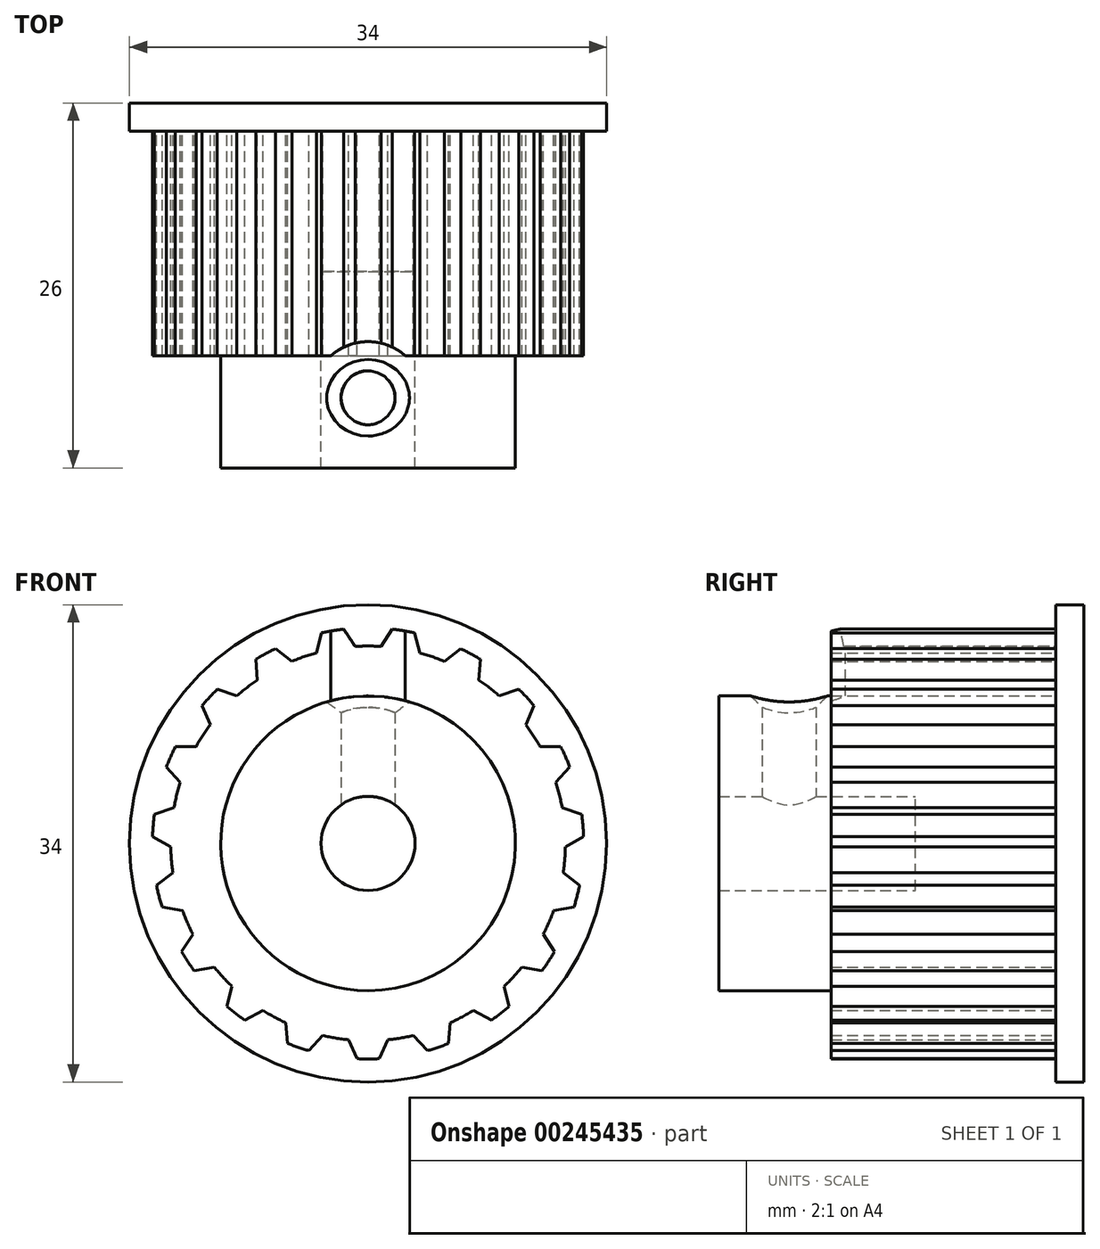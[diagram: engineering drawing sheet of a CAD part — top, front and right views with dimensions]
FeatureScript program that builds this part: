
annotation { "Feature Type Name" : "Feature", "Feature Type Description" : "" }
export const myFeature = defineFeature(function(context is Context, id is Id, definition is map)
    precondition{}
    {
        {
            var Q0;
            Q0=qCreatedBy(makeId("Front.planeOp"),FACE);
            var sketch = newSketch(context, id + "F0", { "sketchPlane" : qUnion([Q0])});
            skArc(sketch, "E0", {"start": v(1.4, -14) * mm, "mid": v(2.31, -13.87) * mm, "end": v(3.22, -13.69) * mm});
            skArc(sketch, "E1", {"start": v(-0.8, -15.34) * mm, "mid": v(0, -15.36) * mm, "end": v(0.8, -15.34) * mm});
            skLineSegment(sketch, "E2", {"start": v(0.8, -15.34) * mm, "end": v(1.4, -14) * mm});
            skLineSegment(sketch, "E3", {"start": v(-0.8, -15.34) * mm, "end": v(-1.4, -14) * mm});
            skArc(sketch, "E4.1.0", {"start": v(4.22, -14.77) * mm, "mid": v(4.99, -14.53) * mm, "end": v(5.74, -14.25) * mm});
            skLineSegment(sketch, "E4.1.1", {"start": v(5.74, -14.25) * mm, "end": v(5.87, -12.78) * mm});
            skLineSegment(sketch, "E4.1.2", {"start": v(4.22, -14.77) * mm, "end": v(3.22, -13.69) * mm});
            skArc(sketch, "E4.2.0", {"start": v(8.8, -12.6) * mm, "mid": v(9.44, -12.12) * mm, "end": v(10.05, -11.61) * mm});
            skLineSegment(sketch, "E4.2.1", {"start": v(10.05, -11.61) * mm, "end": v(9.7, -10.18) * mm});
            skLineSegment(sketch, "E4.2.2", {"start": v(8.8, -12.6) * mm, "end": v(7.5, -11.9) * mm});
            skArc(sketch, "E4.3.0", {"start": v(12.4, -9.06) * mm, "mid": v(12.86, -8.4) * mm, "end": v(13.28, -7.72) * mm});
            skLineSegment(sketch, "E4.3.1", {"start": v(13.28, -7.72) * mm, "end": v(12.48, -6.48) * mm});
            skLineSegment(sketch, "E4.3.2", {"start": v(12.4, -9.06) * mm, "end": v(10.95, -8.82) * mm});
            skArc(sketch, "E4.4.0", {"start": v(14.68, -4.54) * mm, "mid": v(14.9, -3.77) * mm, "end": v(15.07, -3) * mm});
            skLineSegment(sketch, "E4.4.1", {"start": v(15.07, -3) * mm, "end": v(13.9, -2.08) * mm});
            skLineSegment(sketch, "E4.4.2", {"start": v(14.68, -4.54) * mm, "end": v(13.22, -4.8) * mm});
            skArc(sketch, "E4.5.0", {"start": v(15.35, 0.47) * mm, "mid": v(15.3, 1.27) * mm, "end": v(15.22, 2.06) * mm});
            skLineSegment(sketch, "E4.5.1", {"start": v(15.22, 2.06) * mm, "end": v(13.83, 2.55) * mm});
            skLineSegment(sketch, "E4.5.2", {"start": v(15.35, 0.47) * mm, "end": v(14.06, -0.24) * mm});
            skArc(sketch, "E4.6.0", {"start": v(14.37, 5.43) * mm, "mid": v(14.07, 6.17) * mm, "end": v(13.73, 6.9) * mm});
            skLineSegment(sketch, "E4.6.1", {"start": v(13.73, 6.9) * mm, "end": v(12.25, 6.9) * mm});
            skLineSegment(sketch, "E4.6.2", {"start": v(14.37, 5.43) * mm, "end": v(13.38, 4.34) * mm});
            skArc(sketch, "E4.7.0", {"start": v(11.83, 9.8) * mm, "mid": v(11.3, 10.4) * mm, "end": v(10.74, 10.98) * mm});
            skLineSegment(sketch, "E4.7.1", {"start": v(10.74, 10.98) * mm, "end": v(9.35, 10.5) * mm});
            skLineSegment(sketch, "E4.7.2", {"start": v(11.83, 9.8) * mm, "end": v(11.24, 8.45) * mm});
            skArc(sketch, "E4.8.0", {"start": v(8, 13.11) * mm, "mid": v(7.31, 13.51) * mm, "end": v(6.6, 13.87) * mm});
            skLineSegment(sketch, "E4.8.1", {"start": v(6.6, 13.87) * mm, "end": v(5.43, 12.97) * mm});
            skLineSegment(sketch, "E4.8.2", {"start": v(8, 13.11) * mm, "end": v(7.89, 11.64) * mm});
            skArc(sketch, "E4.9.0", {"start": v(3.31, 15) * mm, "mid": v(2.53, 15.15) * mm, "end": v(1.74, 15.26) * mm});
            skLineSegment(sketch, "E4.9.1", {"start": v(1.74, 15.26) * mm, "end": v(0.92, 14.03) * mm});
            skLineSegment(sketch, "E4.9.2", {"start": v(3.31, 15) * mm, "end": v(3.68, 13.57) * mm});
            skArc(sketch, "E4.10.0", {"start": v(-1.74, 15.26) * mm, "mid": v(-2.53, 15.15) * mm, "end": v(-3.31, 15) * mm});
            skLineSegment(sketch, "E4.10.1", {"start": v(-3.31, 15) * mm, "end": v(-3.68, 13.57) * mm});
            skLineSegment(sketch, "E4.10.2", {"start": v(-1.74, 15.26) * mm, "end": v(-0.92, 14.03) * mm});
            skArc(sketch, "E4.11.0", {"start": v(-6.6, 13.87) * mm, "mid": v(-7.31, 13.51) * mm, "end": v(-8, 13.11) * mm});
            skLineSegment(sketch, "E4.11.1", {"start": v(-8, 13.11) * mm, "end": v(-7.89, 11.64) * mm});
            skLineSegment(sketch, "E4.11.2", {"start": v(-6.6, 13.87) * mm, "end": v(-5.43, 12.97) * mm});
            skArc(sketch, "E4.12.0", {"start": v(-10.74, 10.98) * mm, "mid": v(-11.3, 10.4) * mm, "end": v(-11.83, 9.8) * mm});
            skLineSegment(sketch, "E4.12.1", {"start": v(-11.83, 9.8) * mm, "end": v(-11.24, 8.45) * mm});
            skLineSegment(sketch, "E4.12.2", {"start": v(-10.74, 10.98) * mm, "end": v(-9.35, 10.5) * mm});
            skArc(sketch, "E4.13.0", {"start": v(-13.73, 6.9) * mm, "mid": v(-14.07, 6.17) * mm, "end": v(-14.37, 5.43) * mm});
            skLineSegment(sketch, "E4.13.1", {"start": v(-14.37, 5.43) * mm, "end": v(-13.38, 4.34) * mm});
            skLineSegment(sketch, "E4.13.2", {"start": v(-13.73, 6.9) * mm, "end": v(-12.25, 6.9) * mm});
            skArc(sketch, "E4.14.0", {"start": v(-15.22, 2.06) * mm, "mid": v(-15.3, 1.27) * mm, "end": v(-15.35, 0.47) * mm});
            skLineSegment(sketch, "E4.14.1", {"start": v(-15.35, 0.47) * mm, "end": v(-14.06, -0.24) * mm});
            skLineSegment(sketch, "E4.14.2", {"start": v(-15.22, 2.06) * mm, "end": v(-13.83, 2.55) * mm});
            skArc(sketch, "E4.15.0", {"start": v(-15.07, -3) * mm, "mid": v(-14.9, -3.77) * mm, "end": v(-14.68, -4.54) * mm});
            skLineSegment(sketch, "E4.15.1", {"start": v(-14.68, -4.54) * mm, "end": v(-13.22, -4.8) * mm});
            skLineSegment(sketch, "E4.15.2", {"start": v(-15.07, -3) * mm, "end": v(-13.9, -2.08) * mm});
            skArc(sketch, "E4.16.0", {"start": v(-13.28, -7.72) * mm, "mid": v(-12.86, -8.4) * mm, "end": v(-12.4, -9.06) * mm});
            skLineSegment(sketch, "E4.16.1", {"start": v(-12.4, -9.06) * mm, "end": v(-10.95, -8.82) * mm});
            skLineSegment(sketch, "E4.16.2", {"start": v(-13.28, -7.72) * mm, "end": v(-12.48, -6.48) * mm});
            skArc(sketch, "E4.17.0", {"start": v(-10.05, -11.61) * mm, "mid": v(-9.44, -12.12) * mm, "end": v(-8.8, -12.6) * mm});
            skLineSegment(sketch, "E4.17.1", {"start": v(-8.8, -12.6) * mm, "end": v(-7.5, -11.9) * mm});
            skLineSegment(sketch, "E4.17.2", {"start": v(-10.05, -11.61) * mm, "end": v(-9.7, -10.18) * mm});
            skArc(sketch, "E4.18.0", {"start": v(-5.74, -14.25) * mm, "mid": v(-4.99, -14.53) * mm, "end": v(-4.22, -14.77) * mm});
            skLineSegment(sketch, "E4.18.1", {"start": v(-4.22, -14.77) * mm, "end": v(-3.22, -13.69) * mm});
            skLineSegment(sketch, "E4.18.2", {"start": v(-5.74, -14.25) * mm, "end": v(-5.87, -12.78) * mm});
            skArc(sketch, "E5.trimOffspring", {"start": v(5.87, -12.78) * mm, "mid": v(6.7, -12.37) * mm, "end": v(7.5, -11.9) * mm});
            skArc(sketch, "E6.trimOffspring", {"start": v(9.7, -10.18) * mm, "mid": v(10.35, -9.52) * mm, "end": v(10.95, -8.82) * mm});
            skArc(sketch, "E7.trimOffspring", {"start": v(12.48, -6.48) * mm, "mid": v(12.88, -5.65) * mm, "end": v(13.22, -4.8) * mm});
            skArc(sketch, "E8.trimOffspring", {"start": v(-3.22, -13.69) * mm, "mid": v(-2.31, -13.87) * mm, "end": v(-1.4, -14) * mm});
            skArc(sketch, "E9.trimOffspring", {"start": v(-7.5, -11.9) * mm, "mid": v(-6.7, -12.37) * mm, "end": v(-5.87, -12.78) * mm});
            skArc(sketch, "E10.trimOffspring", {"start": v(-10.95, -8.82) * mm, "mid": v(-10.35, -9.52) * mm, "end": v(-9.7, -10.18) * mm});
            skArc(sketch, "E11.trimOffspring", {"start": v(-13.22, -4.8) * mm, "mid": v(-12.88, -5.65) * mm, "end": v(-12.48, -6.48) * mm});
            skArc(sketch, "E12.trimOffspring", {"start": v(-14.06, -0.24) * mm, "mid": v(-14.01, -1.16) * mm, "end": v(-13.9, -2.08) * mm});
            skArc(sketch, "E13.trimOffspring", {"start": v(-13.38, 4.34) * mm, "mid": v(-13.63, 3.45) * mm, "end": v(-13.83, 2.55) * mm});
            skArc(sketch, "E14.trimOffspring", {"start": v(-11.24, 8.45) * mm, "mid": v(-11.77, 7.7) * mm, "end": v(-12.25, 6.9) * mm});
            skArc(sketch, "E15.trimOffspring", {"start": v(-7.89, 11.64) * mm, "mid": v(-8.64, 11.1) * mm, "end": v(-9.35, 10.5) * mm});
            skArc(sketch, "E16.trimOffspring", {"start": v(-3.68, 13.57) * mm, "mid": v(-4.57, 13.3) * mm, "end": v(-5.43, 12.97) * mm});
            skArc(sketch, "E17.trimOffspring", {"start": v(0.92, 14.03) * mm, "mid": v(0, 14.06) * mm, "end": v(-0.92, 14.03) * mm});
            skArc(sketch, "E18.trimOffspring", {"start": v(5.43, 12.97) * mm, "mid": v(4.57, 13.3) * mm, "end": v(3.68, 13.57) * mm});
            skArc(sketch, "E19.trimOffspring", {"start": v(9.35, 10.5) * mm, "mid": v(8.64, 11.1) * mm, "end": v(7.89, 11.64) * mm});
            skArc(sketch, "E20.trimOffspring", {"start": v(12.25, 6.9) * mm, "mid": v(11.77, 7.7) * mm, "end": v(11.24, 8.45) * mm});
            skArc(sketch, "E21.trimOffspring", {"start": v(13.9, -2.08) * mm, "mid": v(14.01, -1.16) * mm, "end": v(14.06, -0.24) * mm});
            skArc(sketch, "E22.trimOffspring", {"start": v(13.83, 2.55) * mm, "mid": v(13.63, 3.45) * mm, "end": v(13.38, 4.34) * mm});
            skSolve(sketch);
        }
        {
            var Q0;
            Q0=qSketchRegion(id+"F0",true);
            extrude(context, id + "F1", {"entities" : qUnion([Q0]), "depth" : 16 * mm});
        }
        {
            var Q0;
            Q0=makeQuery(id+"F1.opExtrude","CAP_FACE",FACE,{"disambiguationData":[OSD([sQuery(id+"F0.wireOp",EDGE,"E0"),sQuery(id+"F0.wireOp",EDGE,"E1"),sQuery(id+"F0.wireOp",EDGE,"E2"),sQuery(id+"F0.wireOp",EDGE,"E3"),sQuery(id+"F0.wireOp",EDGE,"E4.1.0"),sQuery(id+"F0.wireOp",EDGE,"E4.1.1"),sQuery(id+"F0.wireOp",EDGE,"E4.1.2"),sQuery(id+"F0.wireOp",EDGE,"E4.2.0"),sQuery(id+"F0.wireOp",EDGE,"E4.2.1"),sQuery(id+"F0.wireOp",EDGE,"E4.2.2"),sQuery(id+"F0.wireOp",EDGE,"E4.3.0"),sQuery(id+"F0.wireOp",EDGE,"E4.3.1"),sQuery(id+"F0.wireOp",EDGE,"E4.3.2"),sQuery(id+"F0.wireOp",EDGE,"E4.4.0"),sQuery(id+"F0.wireOp",EDGE,"E4.4.1"),sQuery(id+"F0.wireOp",EDGE,"E4.4.2"),sQuery(id+"F0.wireOp",EDGE,"E4.5.0"),sQuery(id+"F0.wireOp",EDGE,"E4.5.1"),sQuery(id+"F0.wireOp",EDGE,"E4.5.2"),sQuery(id+"F0.wireOp",EDGE,"E4.6.0"),sQuery(id+"F0.wireOp",EDGE,"E4.6.1"),sQuery(id+"F0.wireOp",EDGE,"E4.6.2"),sQuery(id+"F0.wireOp",EDGE,"E4.7.0"),sQuery(id+"F0.wireOp",EDGE,"E4.7.1"),sQuery(id+"F0.wireOp",EDGE,"E4.7.2"),sQuery(id+"F0.wireOp",EDGE,"E4.8.0"),sQuery(id+"F0.wireOp",EDGE,"E4.8.1"),sQuery(id+"F0.wireOp",EDGE,"E4.8.2"),sQuery(id+"F0.wireOp",EDGE,"E4.9.0"),sQuery(id+"F0.wireOp",EDGE,"E4.9.1"),sQuery(id+"F0.wireOp",EDGE,"E4.9.2"),sQuery(id+"F0.wireOp",EDGE,"E4.10.0"),sQuery(id+"F0.wireOp",EDGE,"E4.10.1"),sQuery(id+"F0.wireOp",EDGE,"E4.10.2"),sQuery(id+"F0.wireOp",EDGE,"E4.11.0"),sQuery(id+"F0.wireOp",EDGE,"E4.11.1"),sQuery(id+"F0.wireOp",EDGE,"E4.11.2"),sQuery(id+"F0.wireOp",EDGE,"E4.12.0"),sQuery(id+"F0.wireOp",EDGE,"E4.12.1"),sQuery(id+"F0.wireOp",EDGE,"E4.12.2"),sQuery(id+"F0.wireOp",EDGE,"E4.13.0"),sQuery(id+"F0.wireOp",EDGE,"E4.13.1"),sQuery(id+"F0.wireOp",EDGE,"E4.13.2"),sQuery(id+"F0.wireOp",EDGE,"E4.14.0"),sQuery(id+"F0.wireOp",EDGE,"E4.14.1"),sQuery(id+"F0.wireOp",EDGE,"E4.14.2"),sQuery(id+"F0.wireOp",EDGE,"E4.15.0"),sQuery(id+"F0.wireOp",EDGE,"E4.15.1"),sQuery(id+"F0.wireOp",EDGE,"E4.15.2"),sQuery(id+"F0.wireOp",EDGE,"E4.16.0"),sQuery(id+"F0.wireOp",EDGE,"E4.16.1"),sQuery(id+"F0.wireOp",EDGE,"E4.16.2"),sQuery(id+"F0.wireOp",EDGE,"E4.17.0"),sQuery(id+"F0.wireOp",EDGE,"E4.17.1"),sQuery(id+"F0.wireOp",EDGE,"E4.17.2"),sQuery(id+"F0.wireOp",EDGE,"E4.18.0"),sQuery(id+"F0.wireOp",EDGE,"E4.18.1"),sQuery(id+"F0.wireOp",EDGE,"E4.18.2"),sQuery(id+"F0.wireOp",EDGE,"E5.trimOffspring"),sQuery(id+"F0.wireOp",EDGE,"E6.trimOffspring"),sQuery(id+"F0.wireOp",EDGE,"E7.trimOffspring"),sQuery(id+"F0.wireOp",EDGE,"E8.trimOffspring"),sQuery(id+"F0.wireOp",EDGE,"E9.trimOffspring"),sQuery(id+"F0.wireOp",EDGE,"E10.trimOffspring"),sQuery(id+"F0.wireOp",EDGE,"E11.trimOffspring"),sQuery(id+"F0.wireOp",EDGE,"E12.trimOffspring"),sQuery(id+"F0.wireOp",EDGE,"E13.trimOffspring"),sQuery(id+"F0.wireOp",EDGE,"E14.trimOffspring"),sQuery(id+"F0.wireOp",EDGE,"E15.trimOffspring"),sQuery(id+"F0.wireOp",EDGE,"E16.trimOffspring"),sQuery(id+"F0.wireOp",EDGE,"E17.trimOffspring"),sQuery(id+"F0.wireOp",EDGE,"E18.trimOffspring"),sQuery(id+"F0.wireOp",EDGE,"E19.trimOffspring"),sQuery(id+"F0.wireOp",EDGE,"E20.trimOffspring"),sQuery(id+"F0.wireOp",EDGE,"E21.trimOffspring"),sQuery(id+"F0.wireOp",EDGE,"E22.trimOffspring")])],"isStart":true});
            var sketch = newSketch(context, id + "F2", { "sketchPlane" : qUnion([Q0])});
            skCircle(sketch, "E23", {"center": v(0, 0) * mm, "radius": 17 * mm});
            skSolve(sketch);
        }
        {
            var Q0;
            Q0=qSketchRegion(id+"F2",true);
            extrude(context, id + "F3", {"entities" : qUnion([Q0]), "operationType" : NewBodyOperationType.ADD, "depth" : 2 * mm});
        }
        {
            var Q0;
            Q0=makeQuery(id+"F1.opExtrude","CAP_FACE",FACE,{"disambiguationData":[OSD([sQuery(id+"F0.wireOp",EDGE,"E0"),sQuery(id+"F0.wireOp",EDGE,"E1"),sQuery(id+"F0.wireOp",EDGE,"E2"),sQuery(id+"F0.wireOp",EDGE,"E3"),sQuery(id+"F0.wireOp",EDGE,"E4.1.0"),sQuery(id+"F0.wireOp",EDGE,"E4.1.1"),sQuery(id+"F0.wireOp",EDGE,"E4.1.2"),sQuery(id+"F0.wireOp",EDGE,"E4.2.0"),sQuery(id+"F0.wireOp",EDGE,"E4.2.1"),sQuery(id+"F0.wireOp",EDGE,"E4.2.2"),sQuery(id+"F0.wireOp",EDGE,"E4.3.0"),sQuery(id+"F0.wireOp",EDGE,"E4.3.1"),sQuery(id+"F0.wireOp",EDGE,"E4.3.2"),sQuery(id+"F0.wireOp",EDGE,"E4.4.0"),sQuery(id+"F0.wireOp",EDGE,"E4.4.1"),sQuery(id+"F0.wireOp",EDGE,"E4.4.2"),sQuery(id+"F0.wireOp",EDGE,"E4.5.0"),sQuery(id+"F0.wireOp",EDGE,"E4.5.1"),sQuery(id+"F0.wireOp",EDGE,"E4.5.2"),sQuery(id+"F0.wireOp",EDGE,"E4.6.0"),sQuery(id+"F0.wireOp",EDGE,"E4.6.1"),sQuery(id+"F0.wireOp",EDGE,"E4.6.2"),sQuery(id+"F0.wireOp",EDGE,"E4.7.0"),sQuery(id+"F0.wireOp",EDGE,"E4.7.1"),sQuery(id+"F0.wireOp",EDGE,"E4.7.2"),sQuery(id+"F0.wireOp",EDGE,"E4.8.0"),sQuery(id+"F0.wireOp",EDGE,"E4.8.1"),sQuery(id+"F0.wireOp",EDGE,"E4.8.2"),sQuery(id+"F0.wireOp",EDGE,"E4.9.0"),sQuery(id+"F0.wireOp",EDGE,"E4.9.1"),sQuery(id+"F0.wireOp",EDGE,"E4.9.2"),sQuery(id+"F0.wireOp",EDGE,"E4.10.0"),sQuery(id+"F0.wireOp",EDGE,"E4.10.1"),sQuery(id+"F0.wireOp",EDGE,"E4.10.2"),sQuery(id+"F0.wireOp",EDGE,"E4.11.0"),sQuery(id+"F0.wireOp",EDGE,"E4.11.1"),sQuery(id+"F0.wireOp",EDGE,"E4.11.2"),sQuery(id+"F0.wireOp",EDGE,"E4.12.0"),sQuery(id+"F0.wireOp",EDGE,"E4.12.1"),sQuery(id+"F0.wireOp",EDGE,"E4.12.2"),sQuery(id+"F0.wireOp",EDGE,"E4.13.0"),sQuery(id+"F0.wireOp",EDGE,"E4.13.1"),sQuery(id+"F0.wireOp",EDGE,"E4.13.2"),sQuery(id+"F0.wireOp",EDGE,"E4.14.0"),sQuery(id+"F0.wireOp",EDGE,"E4.14.1"),sQuery(id+"F0.wireOp",EDGE,"E4.14.2"),sQuery(id+"F0.wireOp",EDGE,"E4.15.0"),sQuery(id+"F0.wireOp",EDGE,"E4.15.1"),sQuery(id+"F0.wireOp",EDGE,"E4.15.2"),sQuery(id+"F0.wireOp",EDGE,"E4.16.0"),sQuery(id+"F0.wireOp",EDGE,"E4.16.1"),sQuery(id+"F0.wireOp",EDGE,"E4.16.2"),sQuery(id+"F0.wireOp",EDGE,"E4.17.0"),sQuery(id+"F0.wireOp",EDGE,"E4.17.1"),sQuery(id+"F0.wireOp",EDGE,"E4.17.2"),sQuery(id+"F0.wireOp",EDGE,"E4.18.0"),sQuery(id+"F0.wireOp",EDGE,"E4.18.1"),sQuery(id+"F0.wireOp",EDGE,"E4.18.2"),sQuery(id+"F0.wireOp",EDGE,"E5.trimOffspring"),sQuery(id+"F0.wireOp",EDGE,"E6.trimOffspring"),sQuery(id+"F0.wireOp",EDGE,"E7.trimOffspring"),sQuery(id+"F0.wireOp",EDGE,"E8.trimOffspring"),sQuery(id+"F0.wireOp",EDGE,"E9.trimOffspring"),sQuery(id+"F0.wireOp",EDGE,"E10.trimOffspring"),sQuery(id+"F0.wireOp",EDGE,"E11.trimOffspring"),sQuery(id+"F0.wireOp",EDGE,"E12.trimOffspring"),sQuery(id+"F0.wireOp",EDGE,"E13.trimOffspring"),sQuery(id+"F0.wireOp",EDGE,"E14.trimOffspring"),sQuery(id+"F0.wireOp",EDGE,"E15.trimOffspring"),sQuery(id+"F0.wireOp",EDGE,"E16.trimOffspring"),sQuery(id+"F0.wireOp",EDGE,"E17.trimOffspring"),sQuery(id+"F0.wireOp",EDGE,"E18.trimOffspring"),sQuery(id+"F0.wireOp",EDGE,"E19.trimOffspring"),sQuery(id+"F0.wireOp",EDGE,"E20.trimOffspring"),sQuery(id+"F0.wireOp",EDGE,"E21.trimOffspring"),sQuery(id+"F0.wireOp",EDGE,"E22.trimOffspring")])],"isStart":false});
            var sketch = newSketch(context, id + "F4", { "sketchPlane" : qUnion([Q0])});
            skCircle(sketch, "E24", {"center": v(0, 0) * mm, "radius": 3.35 * mm});
            skCircle(sketch, "E25", {"center": v(0, 0) * mm, "radius": 10.5 * mm});
            skSolve(sketch);
        }
        {
            var Q0;
            Q0=qSketchRegion(id+"F4",true);
            extrude(context, id + "F5", {"entities" : qUnion([Q0]), "operationType" : NewBodyOperationType.ADD, "depth" : 8 * mm});
        }
        {
            var Q0;
            Q0=makeQuery(id+"F5.boolean.opBoolean","SPLIT",FACE,{"disambiguationData":[TD([makeQuery(id+"F5.opExtrude","SWEPT_FACE",FACE,{"disambiguationData":[OSD([sQuery(id+"F4.wireOp",EDGE,"E24")])]})])],"derivedFrom":makeQuery(id+"F1.opExtrude","CAP_FACE",FACE,{"disambiguationData":[OSD([sQuery(id+"F0.wireOp",EDGE,"E0"),sQuery(id+"F0.wireOp",EDGE,"E1"),sQuery(id+"F0.wireOp",EDGE,"E2"),sQuery(id+"F0.wireOp",EDGE,"E3"),sQuery(id+"F0.wireOp",EDGE,"E4.1.0"),sQuery(id+"F0.wireOp",EDGE,"E4.1.1"),sQuery(id+"F0.wireOp",EDGE,"E4.1.2"),sQuery(id+"F0.wireOp",EDGE,"E4.2.0"),sQuery(id+"F0.wireOp",EDGE,"E4.2.1"),sQuery(id+"F0.wireOp",EDGE,"E4.2.2"),sQuery(id+"F0.wireOp",EDGE,"E4.3.0"),sQuery(id+"F0.wireOp",EDGE,"E4.3.1"),sQuery(id+"F0.wireOp",EDGE,"E4.3.2"),sQuery(id+"F0.wireOp",EDGE,"E4.4.0"),sQuery(id+"F0.wireOp",EDGE,"E4.4.1"),sQuery(id+"F0.wireOp",EDGE,"E4.4.2"),sQuery(id+"F0.wireOp",EDGE,"E4.5.0"),sQuery(id+"F0.wireOp",EDGE,"E4.5.1"),sQuery(id+"F0.wireOp",EDGE,"E4.5.2"),sQuery(id+"F0.wireOp",EDGE,"E4.6.0"),sQuery(id+"F0.wireOp",EDGE,"E4.6.1"),sQuery(id+"F0.wireOp",EDGE,"E4.6.2"),sQuery(id+"F0.wireOp",EDGE,"E4.7.0"),sQuery(id+"F0.wireOp",EDGE,"E4.7.1"),sQuery(id+"F0.wireOp",EDGE,"E4.7.2"),sQuery(id+"F0.wireOp",EDGE,"E4.8.0"),sQuery(id+"F0.wireOp",EDGE,"E4.8.1"),sQuery(id+"F0.wireOp",EDGE,"E4.8.2"),sQuery(id+"F0.wireOp",EDGE,"E4.9.0"),sQuery(id+"F0.wireOp",EDGE,"E4.9.1"),sQuery(id+"F0.wireOp",EDGE,"E4.9.2"),sQuery(id+"F0.wireOp",EDGE,"E4.10.0"),sQuery(id+"F0.wireOp",EDGE,"E4.10.1"),sQuery(id+"F0.wireOp",EDGE,"E4.10.2"),sQuery(id+"F0.wireOp",EDGE,"E4.11.0"),sQuery(id+"F0.wireOp",EDGE,"E4.11.1"),sQuery(id+"F0.wireOp",EDGE,"E4.11.2"),sQuery(id+"F0.wireOp",EDGE,"E4.12.0"),sQuery(id+"F0.wireOp",EDGE,"E4.12.1"),sQuery(id+"F0.wireOp",EDGE,"E4.12.2"),sQuery(id+"F0.wireOp",EDGE,"E4.13.0"),sQuery(id+"F0.wireOp",EDGE,"E4.13.1"),sQuery(id+"F0.wireOp",EDGE,"E4.13.2"),sQuery(id+"F0.wireOp",EDGE,"E4.14.0"),sQuery(id+"F0.wireOp",EDGE,"E4.14.1"),sQuery(id+"F0.wireOp",EDGE,"E4.14.2"),sQuery(id+"F0.wireOp",EDGE,"E4.15.0"),sQuery(id+"F0.wireOp",EDGE,"E4.15.1"),sQuery(id+"F0.wireOp",EDGE,"E4.15.2"),sQuery(id+"F0.wireOp",EDGE,"E4.16.0"),sQuery(id+"F0.wireOp",EDGE,"E4.16.1"),sQuery(id+"F0.wireOp",EDGE,"E4.16.2"),sQuery(id+"F0.wireOp",EDGE,"E4.17.0"),sQuery(id+"F0.wireOp",EDGE,"E4.17.1"),sQuery(id+"F0.wireOp",EDGE,"E4.17.2"),sQuery(id+"F0.wireOp",EDGE,"E4.18.0"),sQuery(id+"F0.wireOp",EDGE,"E4.18.1"),sQuery(id+"F0.wireOp",EDGE,"E4.18.2"),sQuery(id+"F0.wireOp",EDGE,"E5.trimOffspring"),sQuery(id+"F0.wireOp",EDGE,"E6.trimOffspring"),sQuery(id+"F0.wireOp",EDGE,"E7.trimOffspring"),sQuery(id+"F0.wireOp",EDGE,"E8.trimOffspring"),sQuery(id+"F0.wireOp",EDGE,"E9.trimOffspring"),sQuery(id+"F0.wireOp",EDGE,"E10.trimOffspring"),sQuery(id+"F0.wireOp",EDGE,"E11.trimOffspring"),sQuery(id+"F0.wireOp",EDGE,"E12.trimOffspring"),sQuery(id+"F0.wireOp",EDGE,"E13.trimOffspring"),sQuery(id+"F0.wireOp",EDGE,"E14.trimOffspring"),sQuery(id+"F0.wireOp",EDGE,"E15.trimOffspring"),sQuery(id+"F0.wireOp",EDGE,"E16.trimOffspring"),sQuery(id+"F0.wireOp",EDGE,"E17.trimOffspring"),sQuery(id+"F0.wireOp",EDGE,"E18.trimOffspring"),sQuery(id+"F0.wireOp",EDGE,"E19.trimOffspring"),sQuery(id+"F0.wireOp",EDGE,"E20.trimOffspring"),sQuery(id+"F0.wireOp",EDGE,"E21.trimOffspring"),sQuery(id+"F0.wireOp",EDGE,"E22.trimOffspring")])],"isStart":false})});
            extrude(context, id + "F6", {"entities" : qUnion([Q0]), "operationType" : NewBodyOperationType.REMOVE, "oppositeDirection" : true, "depth" : 6 * mm});
        }
        {
            var Q0;
            Q0=qCreatedBy(makeId("Top.planeOp"),FACE);
            var sketch = newSketch(context, id + "F7", { "sketchPlane" : qUnion([Q0])});
            skLineSegment(sketch, "E26", {"start": v(0, 0) * mm, "end": v(0, -15) * mm});
            skLineSegment(sketch, "E27", {"start": v(0, -15) * mm, "end": v(0, -19) * mm});
            skCircle(sketch, "E28", {"center": v(0, -19) * mm, "radius": 1.93 * mm});
            skSolve(sketch);
        }
        {
            var Q0;
            Q0=qSketchRegion(id+"F7",true);
            extrude(context, id + "F8", {"entities" : qUnion([Q0]), "operationType" : NewBodyOperationType.REMOVE, "depth" : 25 * mm});
        }
        {
            var Q0;
            Q0=makeQuery(id+"F8.boolean.opBoolean","INTERSECT",EDGE,{"derivedFrom":[makeQuery(id+"F5.opExtrude","SWEPT_FACE",FACE,{"disambiguationData":[OSD([sQuery(id+"F4.wireOp",EDGE,"E25")])]}),makeQuery(id+"F8.opExtrude","SWEPT_FACE",FACE,{"disambiguationData":[OSD([sQuery(id+"F7.wireOp",EDGE,"E28")])]})]});
            chamfer(context, id + "F9", {"entities" : qUnion([Q0]), "width" : 0.8 * mm, "tangentPropagation" : true});
        }
        {
            var Q0;
            Q0=qCreatedBy(makeId("Top.planeOp"),FACE);
            cPlane(context, id + "F10", {"entities" : qUnion([Q0]), "cplaneType" : CPlaneType.OFFSET, "offset" : 20 * mm, "width" : 150 * mm, "height" : 150 * mm});
        }
        {
            var Q0;
            Q0=qCreatedBy(id+"F10.planeOp",FACE);
            var sketch = newSketch(context, id + "F11", { "sketchPlane" : qUnion([Q0])});
            skCircle(sketch, "E29", {"center": v(0, -19) * mm, "radius": 4 * mm});
            skSolve(sketch);
        }
        {
            var Q0;
            Q0 = qSketchRegion(id + "F11", true);
            var Q1;
            Q1=makeQuery(id+"F5.opExtrude","SWEPT_FACE",FACE,{"disambiguationData":[OSD([sQuery(id+"F4.wireOp",EDGE,"E25")])]});
            extrude(context, id + "F12", {"entities" : qUnion([Q0]), "operationType" : NewBodyOperationType.REMOVE, "endBound" : BoundingType.UP_TO_SURFACE, "oppositeDirection" : true, "depth" : 25 * mm, "endBoundEntityFace" : qUnion([Q1]), "offsetDistance" : 25 * mm});
        }
    });
